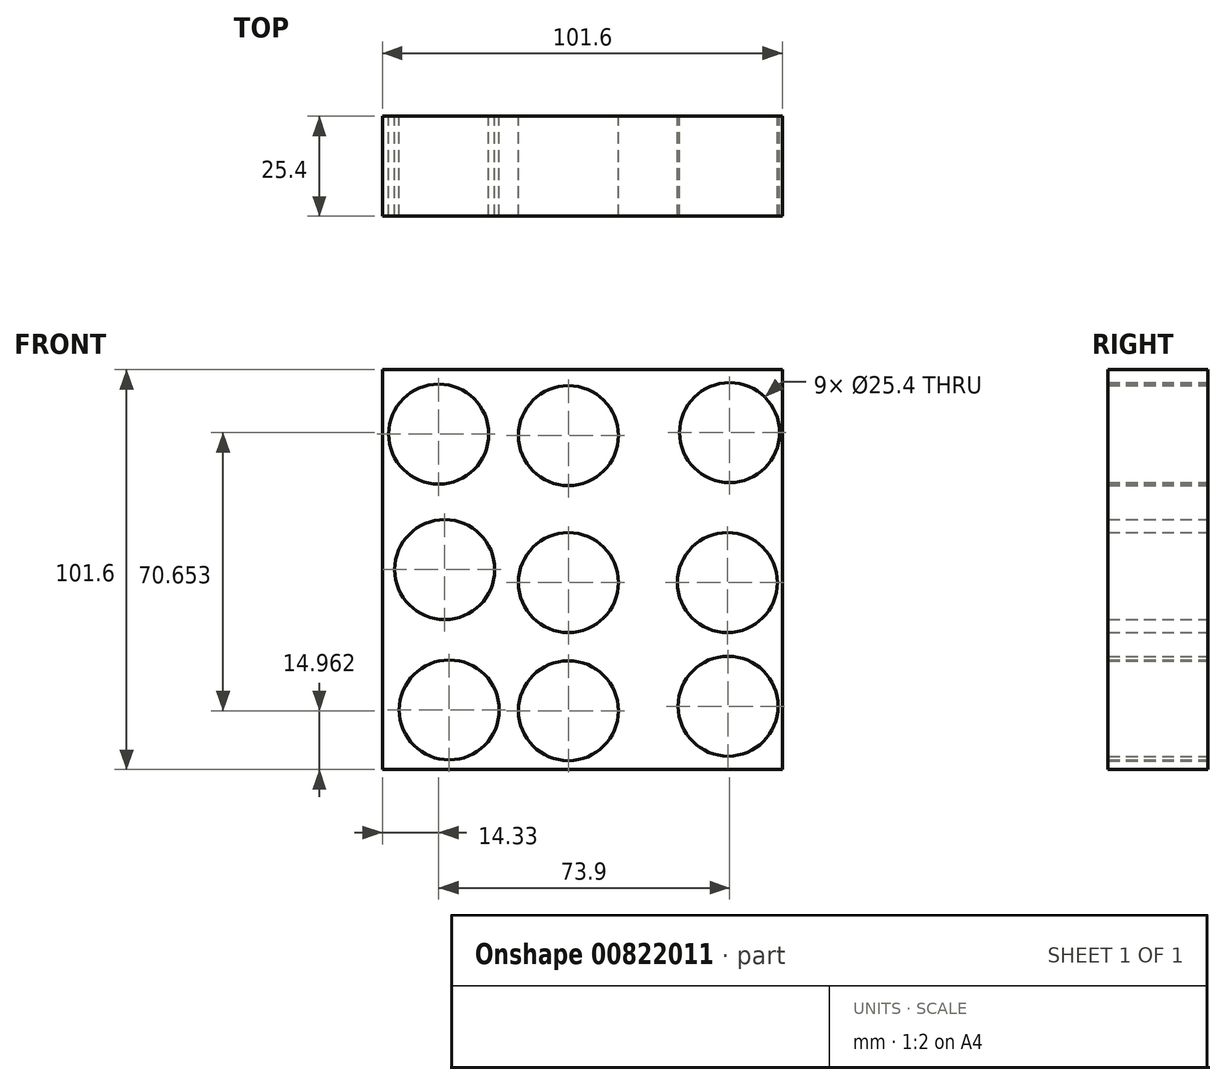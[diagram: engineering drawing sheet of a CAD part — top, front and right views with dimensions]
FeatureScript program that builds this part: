
annotation { "Feature Type Name" : "Feature", "Feature Type Description" : "" }
export const myFeature = defineFeature(function(context is Context, id is Id, definition is map)
    precondition{}
    {
        {
            var Q0;
            Q0=qCreatedBy(makeId("Front.planeOp"),FACE);
            var sketch = newSketch(context, id + "F0", { "sketchPlane" : qUnion([Q0])});
            skLineSegment(sketch, "E0.bottom", {"start": v(-47.27, 54.08) * mm, "end": v(54.33, 54.08) * mm});
            skLineSegment(sketch, "E0.top", {"start": v(-47.27, -47.52) * mm, "end": v(54.33, -47.52) * mm});
            skLineSegment(sketch, "E0.left", {"start": v(-47.27, 54.08) * mm, "end": v(-47.27, -47.52) * mm});
            skLineSegment(sketch, "E0.right", {"start": v(54.33, 54.08) * mm, "end": v(54.33, -47.52) * mm});
            skCircle(sketch, "E1", {"center": v(-32.94, 37.71) * mm, "radius": 12.7 * mm});
            skCircle(sketch, "E2", {"center": v(-31.41, 3.28) * mm, "radius": 12.7 * mm});
            skPoint(sketch, "E2.centerSnap0", {"position": v(-47.27, 3.28) * mm});
            skCircle(sketch, "E3", {"center": v(-30.27, -32.37) * mm, "radius": 12.7 * mm});
            skCircle(sketch, "E4", {"center": v(0, 37.33) * mm, "radius": 12.7 * mm});
            skCircle(sketch, "E5", {"center": v(0, 0) * mm, "radius": 12.7 * mm});
            skCircle(sketch, "E6", {"center": v(40.96, 38.1) * mm, "radius": 12.7 * mm});
            skCircle(sketch, "E7", {"center": v(40.39, 0) * mm, "radius": 12.7 * mm});
            skCircle(sketch, "E8", {"center": v(0, -32.56) * mm, "radius": 12.7 * mm});
            skCircle(sketch, "E9", {"center": v(40.58, -31.41) * mm, "radius": 12.7 * mm});
            skSolve(sketch);
        }
        {
            var Q0;
            Q0=makeQuery(id+"F0.imprint","IMPRINT",FACE,{"disambiguationData":[TD([[makeQuery(id+"F0.imprint","IMPRINT",EDGE,{"derivedFrom":sQuery(id+"F0.wireOp",EDGE,"E0.bottom")}),-1.0]])]});
            extrude(context, id + "F1", {"entities" : qUnion([Q0]), "depth" : 25.4 * mm, "offsetDistance" : 25.4 * mm});
        }
    });
